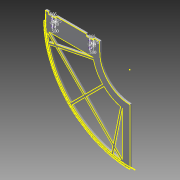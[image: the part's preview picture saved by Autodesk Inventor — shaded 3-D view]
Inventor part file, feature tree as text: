
AUTODESK INVENTOR PART (.ipt)
format: ipt  version: 2013 (Build 170138000, 138)  size: 2,762,752 bytes
history: native  units: mm (DEFAULTED — no unit token found)
features: sketch x9, extrude x8, reference x5, plane x3, other x3
ambient origin geometry x8: Origin, YZ Plane, XZ Plane, XY Plane, X Axis, Y Axis, Z Axis, Center Point
bodies: Solid1 (feature_tree)
feature tree (28):
  extrude  "Extrusion1"  Depth=6.35mm TaperAngle=0.0deg
  plane  "Work Plane1"
  plane  "Work Plane2"
  plane  "Work Plane3"
  other  "Spur Gear"
  extrude  "Extrusion2"  Depth=76.2mm TaperAngle=0.0deg
  extrude  "Extrusion3"  TaperAngle=0.0deg  [1 undecoded]
  extrude  "Extrusion4"  TaperAngle=0.0deg  [1 undecoded]
  extrude  "Extrusion5"  Depth=203.2mm
  extrude  "Extrusion7"  Depth=25.4mm TaperAngle=0.0deg
  extrude  "Extrusion8"  Depth=25.4mm
  extrude  "Extrusion9"  Depth=25.4mm TaperAngle=0.0deg
  sketch  "Sketch1"  dims[d0=582.77125mm d1=6.35mm d2=0.0mm]
  sketch  "Sketch2"  dims[d3=580.39mm d4=76.2mm d5=0.0mm]
  other  "Srf1"
  sketch  "Sketch3"  dims[d6=0.0mm d7=0.068744mm d9=0.0mm]
  sketch  "Sketch4"  dims[d14=0.0mm d15=304.8mm d16=0.0mm]
  sketch  "Sketch5"  dims[d17=0.0mm d18=0.0mm d19=304.8mm d21=203.2mm]
  sketch  "Sketch6"  dims[d22=25.4mm d23=0.0mm d24=25.4mm d25=0.0mm]
  sketch  "Sketch8"  dims[d26=254.0mm d29=25.4mm d30=25.4mm]
  reference  "Reference6"
  sketch  "Sketch10"  dims[d31=558.8mm d32=25.4mm d33=0.0mm]
  reference  "Reference7"
  reference  "Reference8"
  reference  "Reference9"
  reference  "Reference10"
  sketch  "Sketch11"  dims[d36=31.75mm d37=31.75mm d38=184.15mm d39=6.35mm d40=0.0mm d45=0.0mm d46=6.35mm d52=6.35mm d60=6.35mm d61=6.35mm d62=0.0mm d63=90.0deg d64=90.0deg d65=25.4mm d66=0.0mm d67=6.7564mm d68=6.7564mm d69=9.525mm d70=12.7mm d71=19.05mm d72=12.7mm d73=6.7564mm d74=6.7564mm d75=12.7mm d76=9.525mm d77=19.05mm d78=12.704901mm d79=25.4mm d80=0.0mm]
  other  "Pitch Diameter"
note: 2 required parameter values undecoded (feature->parameter linkage not recoverable at this tier; creation-order binding heuristic only, values carry confidence <= 0.55)
